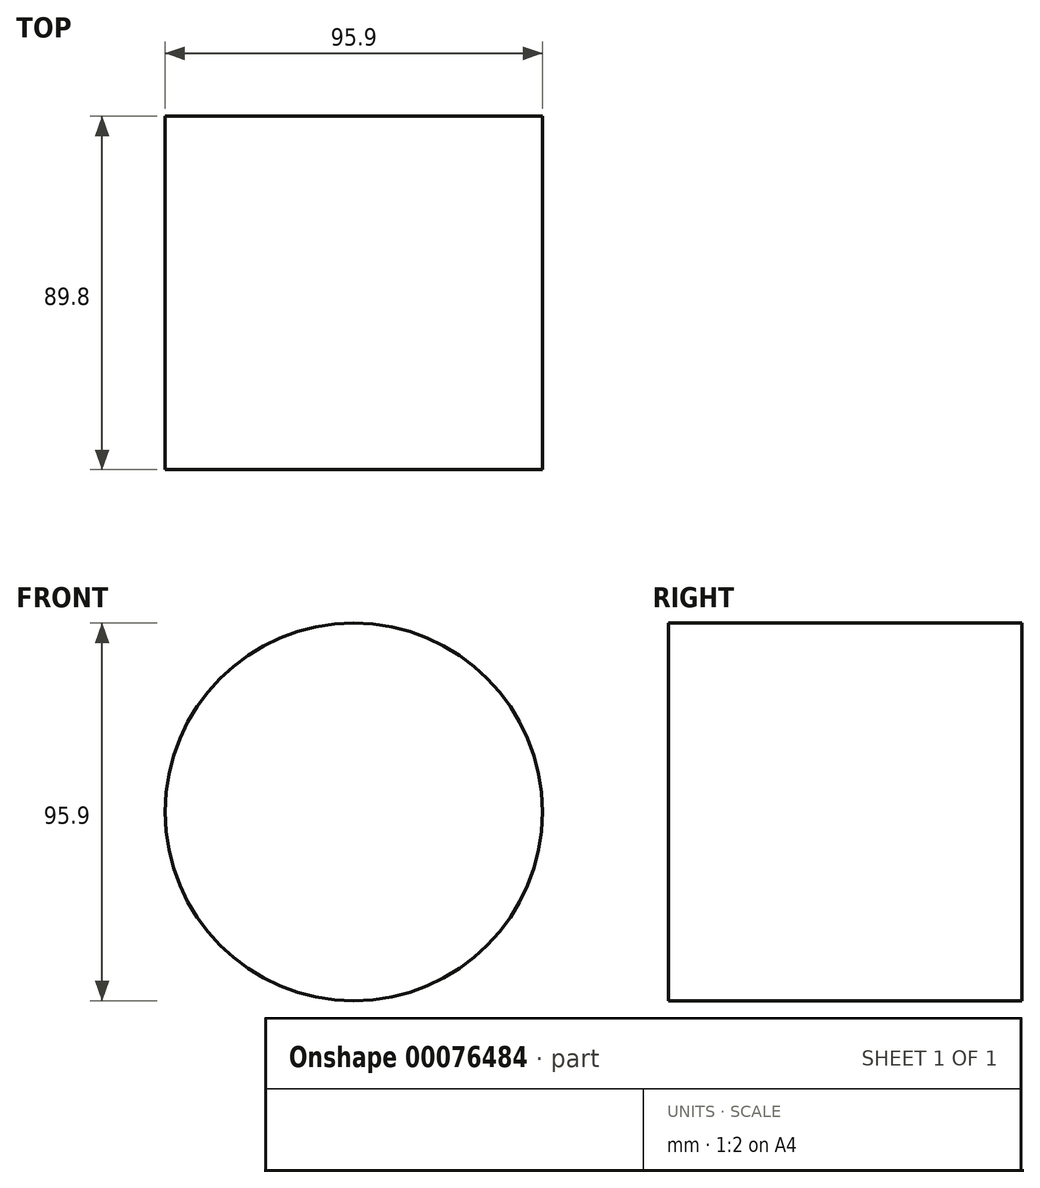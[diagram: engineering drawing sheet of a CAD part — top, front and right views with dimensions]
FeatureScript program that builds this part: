
annotation { "Feature Type Name" : "Feature", "Feature Type Description" : "" }
export const myFeature = defineFeature(function(context is Context, id is Id, definition is map)
    precondition{}
    {
        {
            var Q0;
            Q0=qCreatedBy(makeId("Front.planeOp"),FACE);
            var sketch = newSketch(context, id + "F0", { "sketchPlane" : qUnion([Q0])});
            skCircle(sketch, "E0", {"center": v(0, 0) * mm, "radius": 47.95 * mm});
            skSolve(sketch);
        }
        {
            var Q0;
            Q0=makeQuery(id+"F0.imprint","IMPRINT",FACE,{"disambiguationData":[TD([[makeQuery(id+"F0.imprint","IMPRINT",EDGE,{"derivedFrom":sQuery(id+"F0.wireOp",EDGE,"E0")}),1.0]])]});
            extrude(context, id + "F1", {"entities" : qUnion([Q0]), "depth" : 89.8 * mm});
        }
    });
